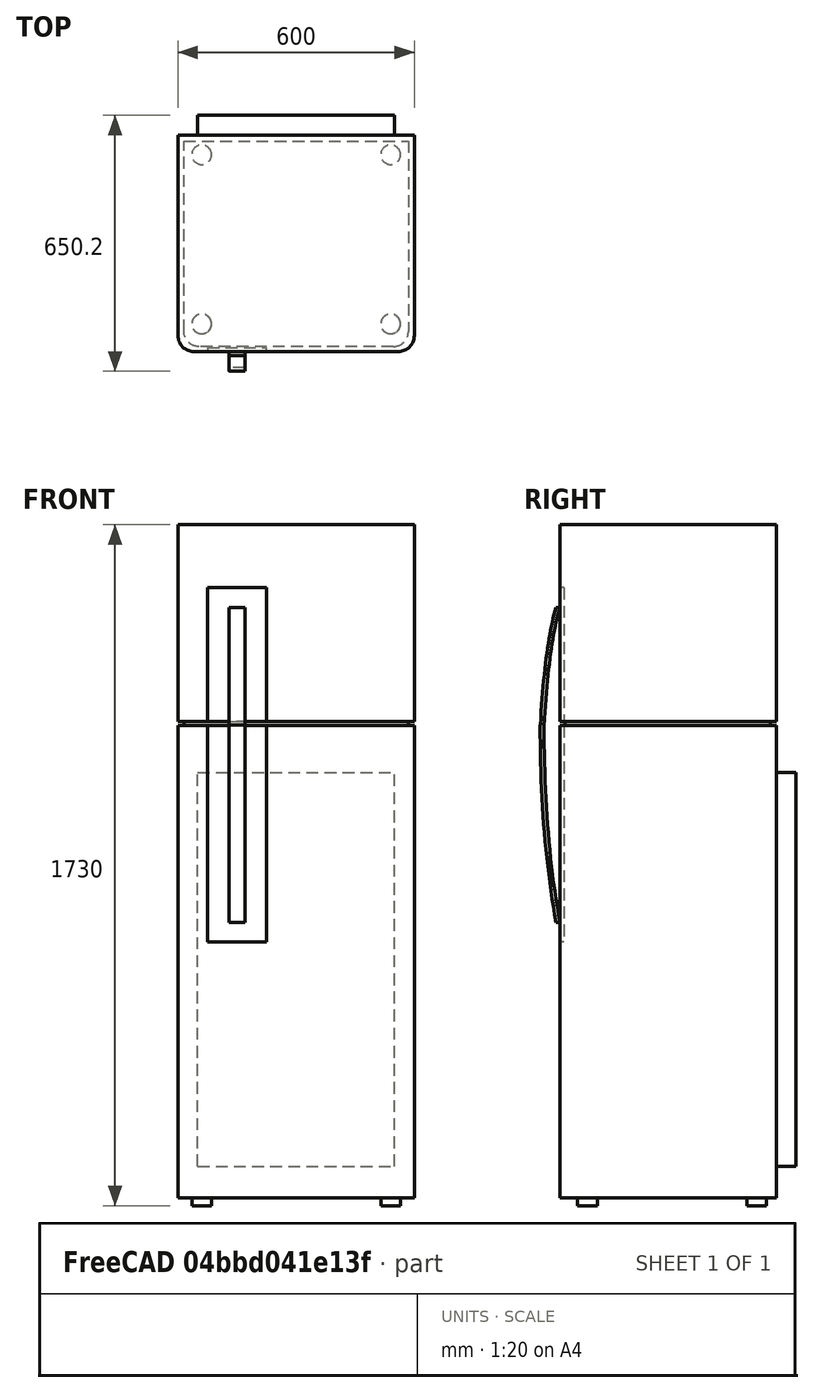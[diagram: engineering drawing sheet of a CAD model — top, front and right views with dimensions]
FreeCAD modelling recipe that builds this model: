
FCSTD DOCUMENT  (FreeCAD 0.16R6706 (Git))
Label: gel
License: All rights reserved
LicenseURL: http://en.wikipedia.org/wiki/All_rights_reserved
objects: Part::Part2DObjectPython×6, Part::Extrusion×6, Part::MultiFuse×5, Part::Fillet×2, Part::Sweep×2, Part::FeaturePython×2, Part::Cut×1, Part::Cylinder×1
note: 25 computed .brp shape members not serialized (recipe doc carries the construction recipe); baked Part::Feature solids carry a one-line shape summary decoded from their .brp

FEATURE [Part::Part2DObjectPython] Rectangle  # Draft 2D object (typed FeaturePython)
  ChamferSize = 0
  Columns = 1
  FilletRadius = 0
  Height = 500
  Length = 600
  MakeFace = true
  Placement = pos=(-300,-100,0) rot=(0,0,1;0rad)
  Rows = 1
FEATURE [Part::Extrusion] Extrusion
  Base = -> Rectangle
  Dir = (0,0,1200)
  Solid = true
FEATURE [Part::Part2DObjectPython] Rectangle001  # Draft 2D object (typed FeaturePython)
  ChamferSize = 0
  Columns = 1
  FilletRadius = 0
  Height = -500
  Length = -600
  MakeFace = true
  Placement = pos=(300,400,1200) rot=(0,0,1;0rad)
  Rows = 1
FEATURE [Part::Extrusion] Extrusion001
  Base = -> Rectangle001
  Dir = (0,0,500)
  Placement = pos=(0,0,10) rot=(0,0,1;0rad)
  Solid = true
FEATURE [Part::Part2DObjectPython] Rectangle002  # Draft 2D object (typed FeaturePython)
  ChamferSize = 0
  Columns = 1
  FilletRadius = 0
  Height = 50
  Length = -600
  MakeFace = true
  Placement = pos=(300,500,0) rot=(0,0,1;0rad)
  Rows = 1
FEATURE [Part::Extrusion] Extrusion002
  Base = -> Rectangle002
  Dir = (0,0,1200)
  Solid = true
FEATURE [Part::Fillet] Fillet
  Base = -> Extrusion002
  Edges = 2 edges r=40: [Edge5,Edge8]
  Placement = pos=(0,-100,0) rot=(0,0,1;0rad)
FEATURE [Part::Part2DObjectPython] Rectangle003  # Draft 2D object (typed FeaturePython)
  ChamferSize = 0
  Columns = 1
  FilletRadius = 0
  Height = 50
  Length = -600
  MakeFace = true
  Placement = pos=(300,500,0) rot=(0,0,1;0rad)
  Rows = 1
FEATURE [Part::Extrusion] Extrusion003
  Base = -> Rectangle003
  Dir = (0,0,500)
  Solid = true
FEATURE [Part::Fillet] Fillet001
  Base = -> Extrusion003
  Edges = 2 edges r=40: [Edge5,Edge8]
  Placement = pos=(0,-100,1210) rot=(0,0,1;0rad)
FEATURE [Part::Sweep] Sweep
  Frenet = false
  Placement = pos=(-150,-200,0) rot=(0,0,1;0rad)
  Solid = true
  Transition = 1
FEATURE [Part::Sweep] Sweep001
  Frenet = false
  Placement = pos=(-150,-200,0) rot=(0,0,1;0rad)
  Solid = true
  Transition = 1
FEATURE [Part::MultiFuse] Fusion
  Shapes = -> [Sweep,Sweep001]
FEATURE [Part::Part2DObjectPython] Rectangle004  # Draft 2D object (typed FeaturePython)
  ChamferSize = 0
  Columns = 1
  FilletRadius = 0
  Height = -900
  Length = -150
  MakeFace = true
  Placement = pos=(-400,0,1600) rot=(1,0,0;1.5708rad)
  Rows = 1
FEATURE [Part::MultiFuse] Fusion001
  Shapes = -> [Fillet001,Fillet]
FEATURE [Part::Extrusion] Extrude
  Base = -> Rectangle004
  Dir = (0,15,0)
  Placement = pos=(625,440,-50) rot=(0,0,1;0rad)
  Solid = false
FEATURE [Part::Cut] Cut
  Base = -> Fusion001
  Tool = -> Extrude
FEATURE [Part::FeaturePython] Clone  label="Clone of Fillet003"  # WARN: FeaturePython — macro-defined, semantics opaque (R4)
  Placement = pos=(0,10,0) rot=(0,0,1;0rad)
  Scale = (0.95,0.95,1)
FEATURE [Part::MultiFuse] Fusion002
  Placement = pos=(0,200,20) rot=(0,0,1;3.14159rad)
  Shapes = -> [Extrusion,Fusion,Extrusion001,Clone,Cut]
FEATURE [Part::Cylinder] Cylinder
  Angle = 360
  Height = 20
  Placement = pos=(-240,-180,0) rot=(0,0,1;0rad)
  Radius = 25
FEATURE [Part::FeaturePython] Array  # Draft array (typed FeaturePython)
  Angle = 360
  ArrayType = 0
  Axis = (0,0,1)
  Base = -> Cylinder
  Center = (0,0,0)
  Fuse = false
  IntervalAxis = (0,0,0)
  IntervalX = (480,0,0)
  IntervalY = (0,430,0)
  IntervalZ = (0,0,0)
  NumberPolar = 1
  NumberX = 2
  NumberY = 2
  NumberZ = 1
FEATURE [Part::MultiFuse] Fusion003
  Shapes = -> [Fusion002,Array]
FEATURE [Part::Part2DObjectPython] Rectangle005  # Draft 2D object (typed FeaturePython)
  ChamferSize = 0
  Columns = 1
  FilletRadius = 0
  Height = 50
  Length = -500
  MakeFace = true
  Placement = pos=(250,300,0) rot=(0,0,1;0rad)
  Rows = 1
FEATURE [Part::Extrusion] Extrusion004
  Base = -> Rectangle005
  Dir = (0,0,1000)
  Placement = pos=(0,0,100) rot=(0,0,1;0rad)
  Solid = true
FEATURE [Part::MultiFuse] Fusion004  label="gel"
  Shapes = -> [Fusion003,Extrusion004]
